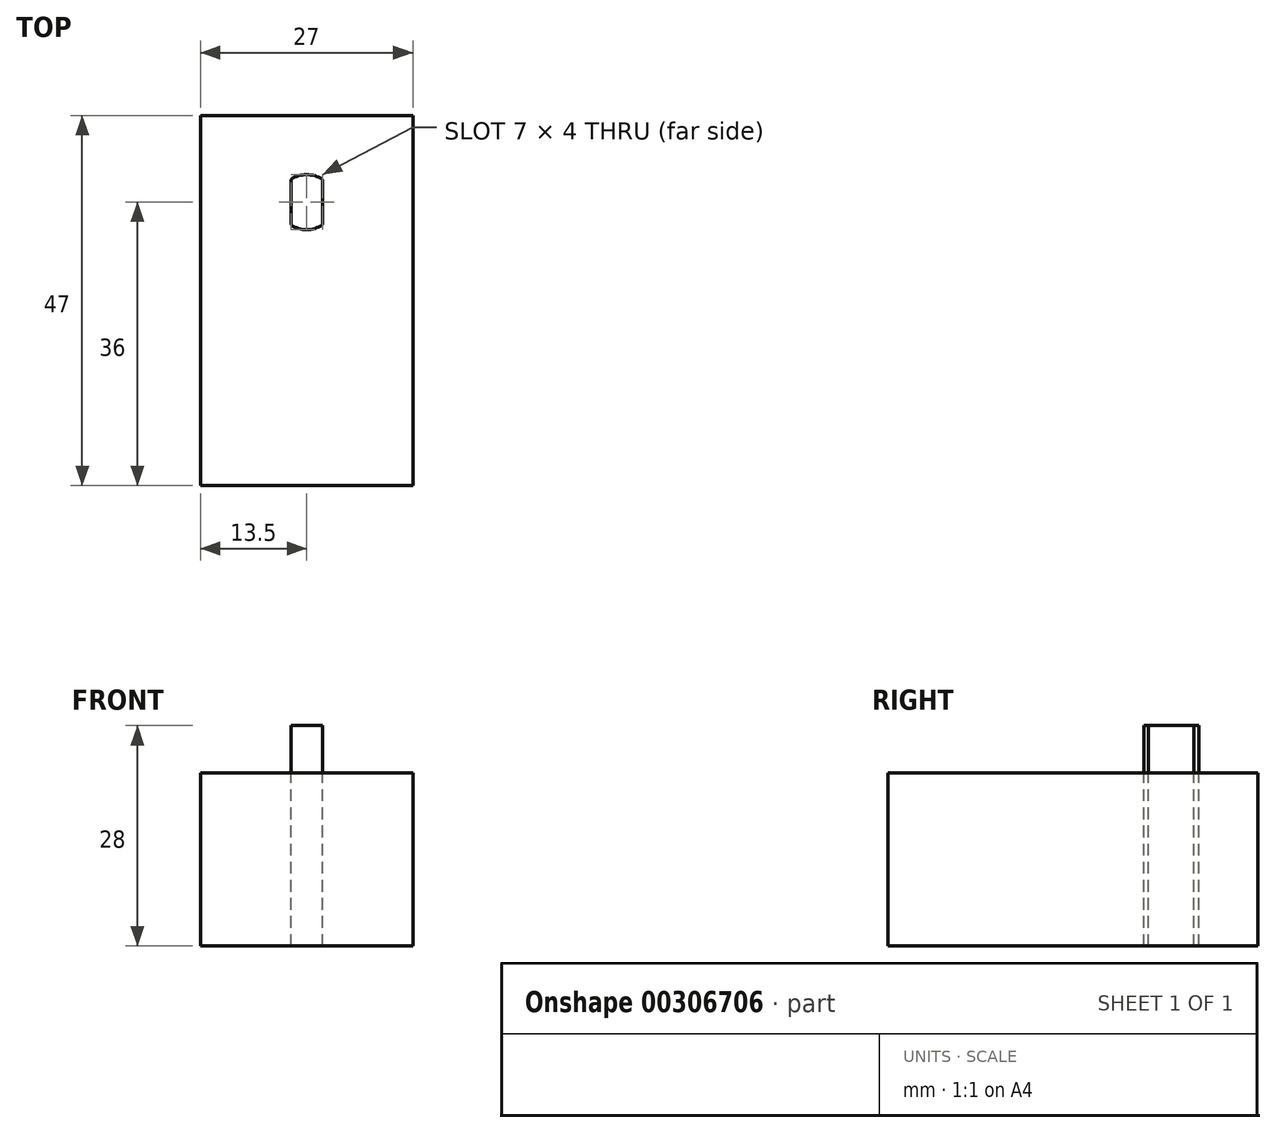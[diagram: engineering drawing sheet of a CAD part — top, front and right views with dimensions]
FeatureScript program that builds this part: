
annotation { "Feature Type Name" : "Feature", "Feature Type Description" : "" }
export const myFeature = defineFeature(function(context is Context, id is Id, definition is map)
    precondition{}
    {
        {
            var Q0;
            Q0=qCreatedBy(makeId("Top.planeOp"),FACE);
            var sketch = newSketch(context, id + "F0", { "sketchPlane" : qUnion([Q0])});
            skLineSegment(sketch, "E0.bottom", {"start": v(13.5, -23.5) * mm, "end": v(-13.5, -23.5) * mm});
            skLineSegment(sketch, "E0.top", {"start": v(13.5, 23.5) * mm, "end": v(-13.5, 23.5) * mm});
            skLineSegment(sketch, "E0.left", {"start": v(13.5, -23.5) * mm, "end": v(13.5, 23.5) * mm});
            skLineSegment(sketch, "E0.right", {"start": v(-13.5, -23.5) * mm, "end": v(-13.5, 23.5) * mm});
            skPoint(sketch, "E0.middle", {"position": v(0, 0) * mm});
            skCircle(sketch, "E1", {"center": v(0, 12.5) * mm, "radius": 9.5 * mm});
            skPoint(sketch, "E1.centerSnap0", {"position": v(0, 23.5) * mm});
            skCircle(sketch, "E2", {"center": v(0, 12.5) * mm, "radius": 3.5 * mm});
            skLineSegment(sketch, "E3", {"start": v(-2, 15.37) * mm, "end": v(-2, 9.63) * mm});
            skLineSegment(sketch, "E4", {"start": v(2, 15.37) * mm, "end": v(2, 9.63) * mm});
            skSolve(sketch);
        }
        {
            var Q0;
            {var subQ0=sQuery(id+"F0.wireOp",EDGE,"E3");Q0=makeQuery(id+"F0.imprint","IMPRINT",FACE,{"disambiguationData":[TD([[makeQuery(id+"F0.imprint","IMPRINT",EDGE,{"derivedFrom":subQ0}),1.0]])]});}
            extrude(context, id + "F1", {"entities" : qUnion([Q0]), "depth" : 6 * mm});
        }
        {
            var Q0;
            Q0=makeQuery(id+"F0.imprint","IMPRINT",FACE,{"disambiguationData":[TD([[makeQuery(id+"F0.imprint","IMPRINT",EDGE,{"derivedFrom":sQuery(id+"F0.wireOp",EDGE,"E0.bottom")}),-1.0]])]});
            var Q1;
            {var subQ0=sQuery(id+"F0.wireOp",EDGE,"E3");Q1=makeQuery(id+"F0.imprint","IMPRINT",FACE,{"disambiguationData":[TD([[makeQuery(id+"F0.imprint","IMPRINT",EDGE,{"derivedFrom":subQ0}),-1.0]])]});}
            var Q2;
            {var subQ0=sQuery(id+"F0.wireOp",EDGE,"E4");Q2=makeQuery(id+"F0.imprint","IMPRINT",FACE,{"disambiguationData":[TD([[makeQuery(id+"F0.imprint","IMPRINT",EDGE,{"derivedFrom":subQ0}),1.0]])]});}
            var Q3;
            Q3=makeQuery(id+"F0.imprint","IMPRINT",FACE,{"disambiguationData":[TD([[makeQuery(id+"F0.imprint","IMPRINT",EDGE,{"derivedFrom":sQuery(id+"F0.wireOp",EDGE,"E1")}),1.0]])]});
            extrude(context, id + "F2", {"entities" : qUnion([Q0, Q1, Q2, Q3]), "depth" : -22 * mm});
        }
        {
            var Q0;
            {var subQ0=sQuery(id+"F0.wireOp",EDGE,"E3");Q0=makeQuery(id+"F0.imprint","IMPRINT",FACE,{"disambiguationData":[TD([[makeQuery(id+"F0.imprint","IMPRINT",EDGE,{"derivedFrom":subQ0}),1.0]])]});}
            extrude(context, id + "F3", {"entities" : qUnion([Q0]), "depth" : -22 * mm});
        }
    });
